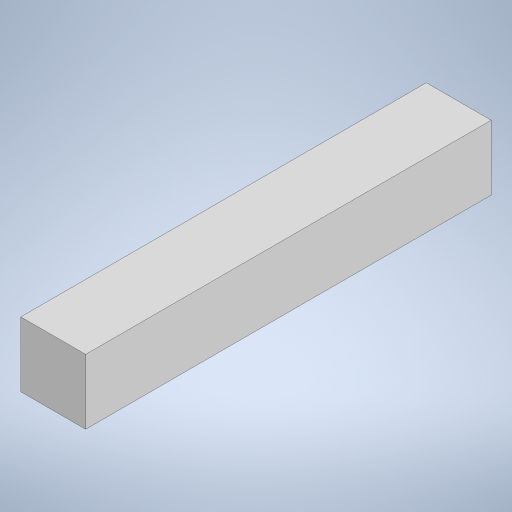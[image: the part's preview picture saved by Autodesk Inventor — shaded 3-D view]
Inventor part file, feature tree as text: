
AUTODESK INVENTOR PART (.ipt)
format: ipt  version: 2024 (Build 280153000, 153)  size: 200,704 bytes
history: native  units: in
note: dims shown in document units (in); Inventor stores cm internally (conversion verified against a paired STEP export)
features: extrude x1, sketch x1
ambient origin geometry x8: Origin, YZ Plane, XZ Plane, XY Plane, X Axis, Y Axis, Z Axis, Center Point
bodies: Solid1 (feature_tree)
feature tree (2):
  extrude  "Extrusion1"  Depth=1.0in
  sketch  "Sketch1"  dims[d0=6.25in d1=1.0in d2=1.0in d3=0.0in]
